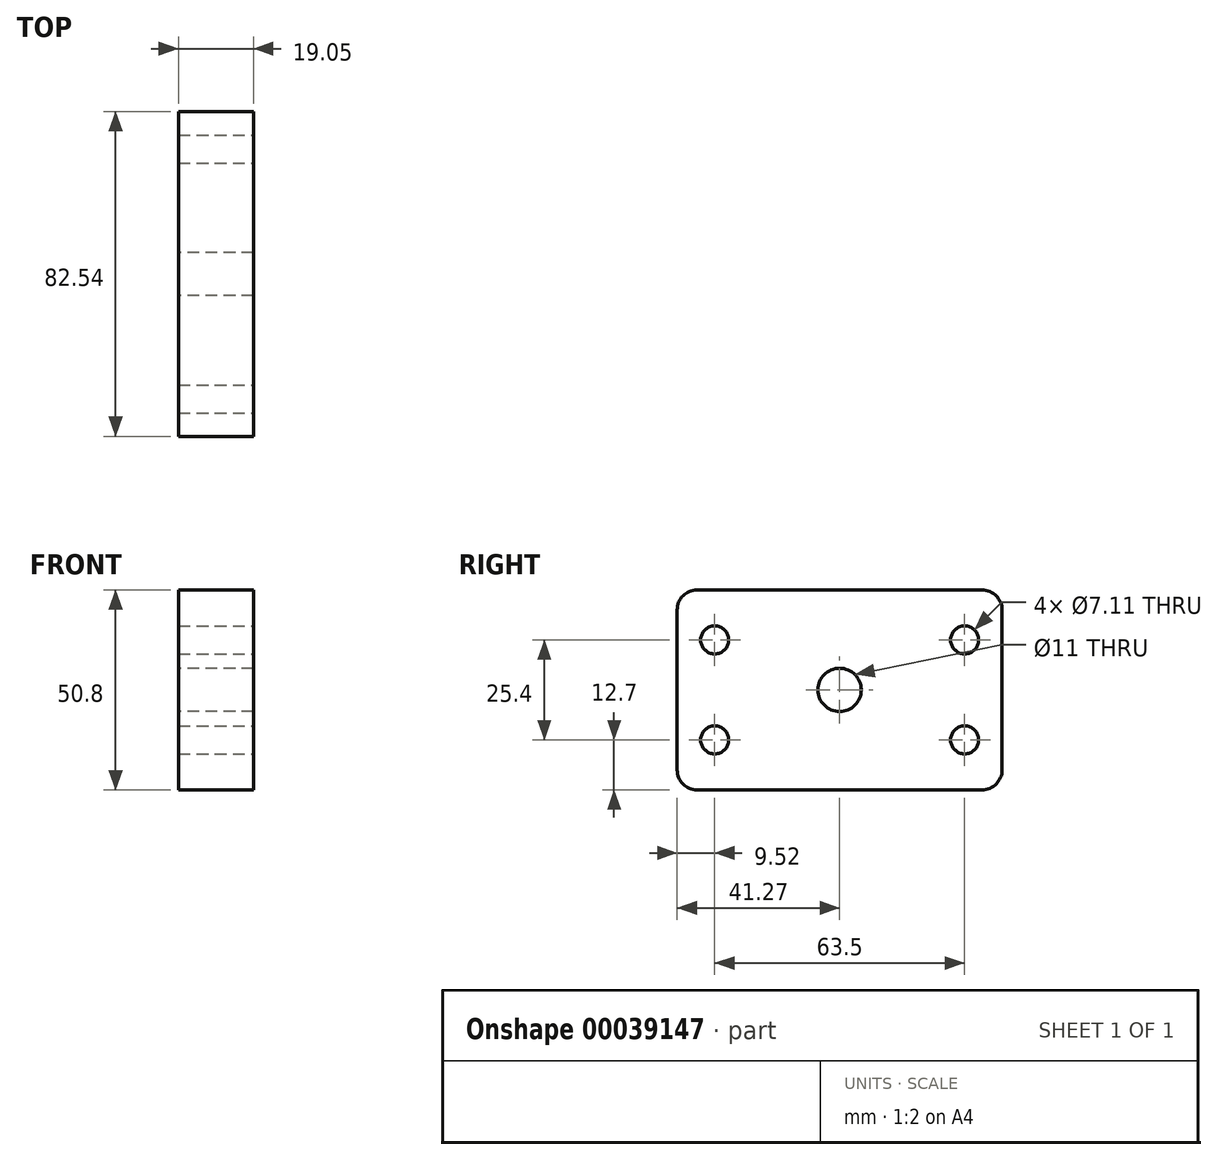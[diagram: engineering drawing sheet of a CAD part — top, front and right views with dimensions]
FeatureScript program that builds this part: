
annotation { "Feature Type Name" : "Feature", "Feature Type Description" : "" }
export const myFeature = defineFeature(function(context is Context, id is Id, definition is map)
    precondition{}
    {
        {
            var Q0;
            Q0=qCreatedBy(makeId("Right.planeOp"),FACE);
            var sketch = newSketch(context, id + "F0", { "sketchPlane" : qUnion([Q0])});
            skCircle(sketch, "E0", {"center": v(0, 0) * mm, "radius": 5.5 * mm});
            skLineSegment(sketch, "E1.rect.bottom", {"start": v(-41.27, 25.4) * mm, "end": v(41.28, 25.4) * mm});
            skLineSegment(sketch, "E1.rect.top", {"start": v(-41.28, -25.4) * mm, "end": v(41.27, -25.4) * mm});
            skLineSegment(sketch, "E1.rect.left", {"start": v(-41.27, 25.4) * mm, "end": v(-41.28, -25.4) * mm});
            skLineSegment(sketch, "E1.rect.right", {"start": v(41.28, 25.4) * mm, "end": v(41.27, -25.4) * mm});
            skSolve(sketch);
        }
        {
            var Q0;
            Q0=makeQuery(id+"F0.imprint","IMPRINT",FACE,{"disambiguationData":[TD([[makeQuery(id+"F0.imprint","IMPRINT",EDGE,{"derivedFrom":sQuery(id+"F0.wireOp",EDGE,"E0")}),-1.0]])]});
            extrude(context, id + "F1", {"entities" : qUnion([Q0]), "depth" : 19.05 * mm});
        }
        {
            var Q0;
            Q0=makeQuery(id+"F1.opExtrude","CAP_FACE",FACE,{"disambiguationData":[OSD([sQuery(id+"F0.wireOp",EDGE,"E0"),sQuery(id+"F0.wireOp",EDGE,"E1.rect.bottom"),sQuery(id+"F0.wireOp",EDGE,"E1.rect.top"),sQuery(id+"F0.wireOp",EDGE,"E1.rect.left"),sQuery(id+"F0.wireOp",EDGE,"E1.rect.right")])],"isStart":false});
            var sketch = newSketch(context, id + "F2", { "sketchPlane" : qUnion([Q0])});
            skLineSegment(sketch, "E2.bottom", {"start": v(-31.75, 12.7) * mm, "end": v(31.75, 12.7) * mm, "construction": true});
            skLineSegment(sketch, "E2.top", {"start": v(-31.75, -12.7) * mm, "end": v(31.75, -12.7) * mm, "construction": true});
            skLineSegment(sketch, "E2.left", {"start": v(-31.75, 12.7) * mm, "end": v(-31.75, -12.7) * mm, "construction": true});
            skLineSegment(sketch, "E2.right", {"start": v(31.75, 12.7) * mm, "end": v(31.75, -12.7) * mm, "construction": true});
            skLineSegment(sketch, "E3", {"start": v(0, 0) * mm, "end": v(0, 12.7) * mm, "construction": true});
            skLineSegment(sketch, "E4", {"start": v(2, 0) * mm, "end": v(31.75, 0) * mm, "construction": true});
            skPoint(sketch, "E5", {"position": v(-31.75, 12.7) * mm});
            skPoint(sketch, "E6", {"position": v(31.75, 12.7) * mm});
            skPoint(sketch, "E7", {"position": v(31.75, -12.7) * mm});
            skPoint(sketch, "E8", {"position": v(-31.75, -12.7) * mm});
            skSolve(sketch);
        }
        {
            var Q0;
            Q0=sQuery(id+"F2.wireOp",VERTEX,"E5");
            var Q1;
            Q1=sQuery(id+"F2.wireOp",VERTEX,"E6");
            var Q2;
            Q2=sQuery(id+"F2.wireOp",VERTEX,"E7");
            var Q3;
            Q3=sQuery(id+"F2.wireOp",VERTEX,"E8");
            var Q4;
            Q4=makeQuery(id+"F1.opExtrude","SWEPT_BODY",BODY,{"disambiguationData":[OSD([sQuery(id+"F0.wireOp",EDGE,"E0"),sQuery(id+"F0.wireOp",EDGE,"E1.rect.bottom"),sQuery(id+"F0.wireOp",EDGE,"E1.rect.top"),sQuery(id+"F0.wireOp",EDGE,"E1.rect.left"),sQuery(id+"F0.wireOp",EDGE,"E1.rect.right")])]});
            hole(context, id + "F3", {"style" : HoleStyle.SIMPLE, "holeDiameter" : 7.11 * mm, "endStyle" : HoleEndStyle.THROUGH, "locations" : qUnion([Q0, Q1, Q2, Q3]), "scope" : qUnion([Q4])});
        }
        {
            var Q0;
            Q0=makeQuery(id+"F1.opExtrude","SWEPT_EDGE",EDGE,{"disambiguationData":[OSD([sQuery(id+"F0.wireOp",EDGE,"E1.rect.bottom"),sQuery(id+"F0.wireOp",EDGE,"E1.rect.left")])]});
            var Q1;
            Q1=makeQuery(id+"F1.opExtrude","SWEPT_EDGE",EDGE,{"disambiguationData":[OSD([sQuery(id+"F0.wireOp",EDGE,"E1.rect.top"),sQuery(id+"F0.wireOp",EDGE,"E1.rect.left")])]});
            var Q2;
            Q2=makeQuery(id+"F1.opExtrude","SWEPT_EDGE",EDGE,{"disambiguationData":[OSD([sQuery(id+"F0.wireOp",EDGE,"E1.rect.top"),sQuery(id+"F0.wireOp",EDGE,"E1.rect.right")])]});
            var Q3;
            Q3=makeQuery(id+"F1.opExtrude","SWEPT_EDGE",EDGE,{"disambiguationData":[OSD([sQuery(id+"F0.wireOp",EDGE,"E1.rect.bottom"),sQuery(id+"F0.wireOp",EDGE,"E1.rect.right")])]});
            fillet(context, id + "F4", {"entities" : qUnion([Q0, Q1, Q2, Q3]), "radius" : 5.08 * mm, "tangentPropagation" : true, "allowEdgeOverflow" : false});
        }
    });
